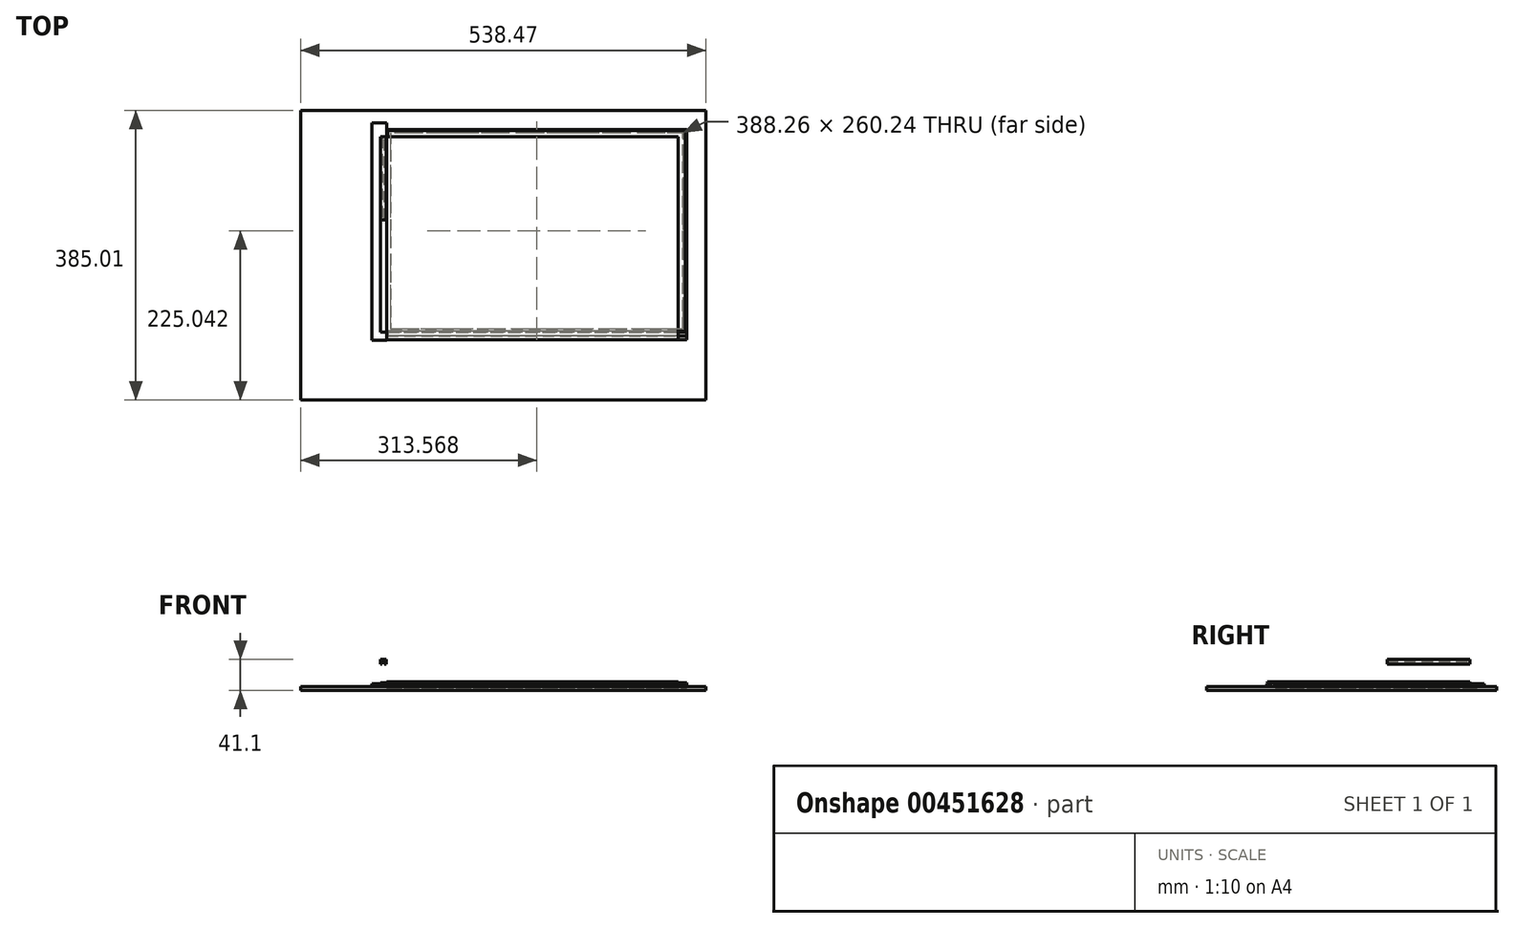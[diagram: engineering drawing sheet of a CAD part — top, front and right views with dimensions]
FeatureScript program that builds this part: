
annotation { "Feature Type Name" : "Feature", "Feature Type Description" : "" }
export const myFeature = defineFeature(function(context is Context, id is Id, definition is map)
    precondition{}
    {
        {
            var Q0;
            Q0=qCreatedBy(makeId("Top.planeOp"),FACE);
            var sketch = newSketch(context, id + "F0", { "sketchPlane" : qUnion([Q0])});
            skLineSegment(sketch, "E0", {"start": v(-190.36, 104.66) * mm, "end": v(205.64, 104.66) * mm});
            skLineSegment(sketch, "E1", {"start": v(205.64, 104.66) * mm, "end": v(205.64, -154.94) * mm});
            skLineSegment(sketch, "E2", {"start": v(205.64, -154.94) * mm, "end": v(-190.27, -154.94) * mm});
            skLineSegment(sketch, "E3", {"start": v(-190.27, -154.94) * mm, "end": v(-190.27, 104.66) * mm});
            skSolve(sketch);
        }
        {
            var Q0;
            Q0 = qSketchRegion(id + "F0", true);
            extrude(context, id + "F1", {"entities" : qUnion([Q0]), "depth" : 1.1 * mm});
        }
        {
            var Q0;
            Q0=makeQuery(id+"F1.opExtrude","CAP_FACE",FACE,{"disambiguationData":[OSD([sQuery(id+"F0.wireOp",EDGE,"E0"),sQuery(id+"F0.wireOp",EDGE,"E1"),sQuery(id+"F0.wireOp",EDGE,"E2"),sQuery(id+"F0.wireOp",EDGE,"E3")])],"isStart":false});
            var sketch = newSketch(context, id + "F2", { "sketchPlane" : qUnion([Q0])});
            skLineSegment(sketch, "E4", {"start": v(-181.96, 104.66) * mm, "end": v(-181.96, -164.94) * mm});
            skLineSegment(sketch, "E5", {"start": v(-181.96, -164.94) * mm, "end": v(205.64, -164.94) * mm});
            skLineSegment(sketch, "E6", {"start": v(205.64, -164.94) * mm, "end": v(205.64, 104.66) * mm});
            skLineSegment(sketch, "E7", {"start": v(205.64, 104.66) * mm, "end": v(-181.96, 104.66) * mm});
            skSolve(sketch);
        }
        {
            var Q0;
            Q0 = qSketchRegion(id + "F2", true);
            extrude(context, id + "F3", {"entities" : qUnion([Q0]), "depth" : 1.1 * mm});
        }
        {
            var Q0;
            Q0=makeQuery(id+"F1.opExtrude","CAP_FACE",FACE,{"disambiguationData":[OSD([sQuery(id+"F0.wireOp",EDGE,"E0"),sQuery(id+"F0.wireOp",EDGE,"E1"),sQuery(id+"F0.wireOp",EDGE,"E2"),sQuery(id+"F0.wireOp",EDGE,"E3")])],"isStart":true});
            cPlane(context, id + "F4", {"entities" : qUnion([Q0]), "cplaneType" : CPlaneType.OFFSET, "offset" : 9 * mm, "width" : 150 * mm, "height" : 150 * mm});
        }
        {
            var Q0;
            Q0=qCreatedBy(id+"F4.planeOp",FACE);
            var sketch = newSketch(context, id + "F5", { "sketchPlane" : qUnion([Q0])});
            skLineSegment(sketch, "E8", {"start": v(-296.19, 245.18) * mm, "end": v(242.28, 245.18) * mm});
            skLineSegment(sketch, "E9", {"start": v(242.28, 245.18) * mm, "end": v(242.28, -139.83) * mm});
            skLineSegment(sketch, "E10", {"start": v(242.28, -139.83) * mm, "end": v(-296.19, -139.83) * mm});
            skLineSegment(sketch, "E11", {"start": v(-296.19, -139.83) * mm, "end": v(-296.19, 245.18) * mm});
            skLineSegment(sketch, "E12", {"start": v(-181.87, 154.91) * mm, "end": v(216.63, 154.91) * mm});
            skLineSegment(sketch, "E13", {"start": v(216.63, 154.91) * mm, "end": v(216.63, -114.17) * mm});
            skLineSegment(sketch, "E14", {"start": v(216.63, -114.17) * mm, "end": v(-181.87, -114.17) * mm});
            skLineSegment(sketch, "E15", {"start": v(-181.87, -114.17) * mm, "end": v(-181.87, 154.91) * mm});
            skLineSegment(sketch, "E16", {"start": v(-176.75, 150.26) * mm, "end": v(211.5, 150.26) * mm});
            skLineSegment(sketch, "E17", {"start": v(211.5, 150.26) * mm, "end": v(211.5, -109.98) * mm});
            skLineSegment(sketch, "E18", {"start": v(211.5, -109.98) * mm, "end": v(-176.75, -109.98) * mm});
            skLineSegment(sketch, "E19", {"start": v(-176.75, -109.98) * mm, "end": v(-176.75, 150.26) * mm});
            skSolve(sketch);
        }
        {
            var Q0;
            Q0=makeQuery(id+"F5.imprint","IMPRINT",FACE,{"disambiguationData":[TD([[makeQuery(id+"F5.imprint","IMPRINT",EDGE,{"derivedFrom":sQuery(id+"F5.wireOp",EDGE,"E8")}),-1.0]])]});
            extrude(context, id + "F6", {"entities" : qUnion([Q0]), "oppositeDirection" : true, "depth" : 5 * mm});
        }
        {
            var Q0;
            Q0=makeQuery(id+"F5.imprint","IMPRINT",FACE,{"disambiguationData":[TD([[makeQuery(id+"F5.imprint","IMPRINT",EDGE,{"derivedFrom":sQuery(id+"F5.wireOp",EDGE,"E12")}),-1.0]])]});
            extrude(context, id + "F7", {"entities" : qUnion([Q0]), "operationType" : NewBodyOperationType.ADD, "oppositeDirection" : true, "depth" : 3 * mm});
        }
        {
            var Q0;
            Q0=makeQuery(id+"F6.opExtrude","CAP_FACE",FACE,{"disambiguationData":[OSD([sQuery(id+"F5.wireOp",EDGE,"E8"),sQuery(id+"F5.wireOp",EDGE,"E9"),sQuery(id+"F5.wireOp",EDGE,"E10"),sQuery(id+"F5.wireOp",EDGE,"E11"),sQuery(id+"F5.wireOp",EDGE,"E12"),sQuery(id+"F5.wireOp",EDGE,"E13"),sQuery(id+"F5.wireOp",EDGE,"E14"),sQuery(id+"F5.wireOp",EDGE,"E15")])],"isStart":false});
            var sketch = newSketch(context, id + "F8", { "sketchPlane" : qUnion([Q0])});
            skLineSegment(sketch, "E20", {"start": v(-181.87, -165.6) * mm, "end": v(-201.72, -165.6) * mm});
            skLineSegment(sketch, "E21", {"start": v(-201.72, -165.6) * mm, "end": v(-201.72, 123.46) * mm});
            skLineSegment(sketch, "E22", {"start": v(-201.72, 123.46) * mm, "end": v(-181.87, 123.46) * mm});
            skLineSegment(sketch, "E23", {"start": v(-181.87, 123.46) * mm, "end": v(-181.87, -165.6) * mm});
            skSolve(sketch);
        }
        {
            var Q0;
            {var subQ3=sQuery(id+"F8.wireOp",EDGE,"E20");Q0=makeQuery(id+"F8.imprint","IMPRINT",FACE,{"disambiguationData":[TD([[makeQuery(id+"F8.imprint","IMPRINT",EDGE,{"derivedFrom":subQ3}),-1.0]])]});}
            extrude(context, id + "F9", {"entities" : qUnion([Q0]), "depth" : 4 * mm});
        }
        {
            var Q0;
            Q0=makeQuery(id+"F6.opExtrude","CAP_FACE",FACE,{"disambiguationData":[OSD([sQuery(id+"F5.wireOp",EDGE,"E8"),sQuery(id+"F5.wireOp",EDGE,"E9"),sQuery(id+"F5.wireOp",EDGE,"E10"),sQuery(id+"F5.wireOp",EDGE,"E11"),sQuery(id+"F5.wireOp",EDGE,"E12"),sQuery(id+"F5.wireOp",EDGE,"E13"),sQuery(id+"F5.wireOp",EDGE,"E14"),sQuery(id+"F5.wireOp",EDGE,"E15")])],"isStart":false});
            var sketch = newSketch(context, id + "F10", { "sketchPlane" : qUnion([Q0])});
            skLineSegment(sketch, "E24", {"start": v(-181.55, -160.24) * mm, "end": v(216.92, -160.24) * mm});
            skLineSegment(sketch, "E25", {"start": v(216.92, -160.24) * mm, "end": v(216.92, -165.22) * mm});
            skLineSegment(sketch, "E26", {"start": v(216.92, -165.22) * mm, "end": v(-181.55, -165.22) * mm});
            skLineSegment(sketch, "E27", {"start": v(-181.55, -165.22) * mm, "end": v(-181.55, -160.24) * mm});
            skSolve(sketch);
        }
        {
            var Q0;
            Q0=makeQuery(id+"F10.imprint","IMPRINT",FACE,{"disambiguationData":[TD([[makeQuery(id+"F10.imprint","IMPRINT",EDGE,{"derivedFrom":sQuery(id+"F10.wireOp",EDGE,"E24")}),-1.0]])]});
            extrude(context, id + "F11", {"entities" : qUnion([Q0]), "depth" : 3 * mm});
        }
        {
            var Q0;
            Q0=makeQuery(id+"F7.opExtrude","CAP_FACE",FACE,{"disambiguationData":[OSD([sQuery(id+"F5.wireOp",EDGE,"E12"),sQuery(id+"F5.wireOp",EDGE,"E13"),sQuery(id+"F5.wireOp",EDGE,"E14"),sQuery(id+"F5.wireOp",EDGE,"E15"),sQuery(id+"F5.wireOp",EDGE,"E16"),sQuery(id+"F5.wireOp",EDGE,"E17"),sQuery(id+"F5.wireOp",EDGE,"E18"),sQuery(id+"F5.wireOp",EDGE,"E19")])],"isStart":false});
            var sketch = newSketch(context, id + "F12", { "sketchPlane" : qUnion([Q0])});
            skLineSegment(sketch, "E28", {"start": v(-180.71, 112.97) * mm, "end": v(215.2, 112.97) * mm});
            skLineSegment(sketch, "E29", {"start": v(215.2, 112.97) * mm, "end": v(215.2, -153.74) * mm});
            skLineSegment(sketch, "E30", {"start": v(215.2, -153.74) * mm, "end": v(-180.71, -153.74) * mm});
            skLineSegment(sketch, "E31", {"start": v(-180.71, -153.74) * mm, "end": v(-180.71, 112.97) * mm});
            skSolve(sketch);
        }
        {
            var Q0;
            Q0 = qSketchRegion(id + "F12", true);
            extrude(context, id + "F13", {"entities" : qUnion([Q0]), "depth" : 6 * mm});
        }
        {
            var Q0;
            Q0=makeQuery(id+"F6.opExtrude","CAP_FACE",FACE,{"disambiguationData":[OSD([sQuery(id+"F5.wireOp",EDGE,"E8"),sQuery(id+"F5.wireOp",EDGE,"E9"),sQuery(id+"F5.wireOp",EDGE,"E10"),sQuery(id+"F5.wireOp",EDGE,"E11"),sQuery(id+"F5.wireOp",EDGE,"E12"),sQuery(id+"F5.wireOp",EDGE,"E13"),sQuery(id+"F5.wireOp",EDGE,"E14"),sQuery(id+"F5.wireOp",EDGE,"E15")])],"isStart":false});
            var sketch = newSketch(context, id + "F14", { "sketchPlane" : qUnion([Q0])});
            skLineSegment(sketch, "E32", {"start": v(-180.01, -159.95) * mm, "end": v(-180.01, -155.07) * mm});
            skLineSegment(sketch, "E33", {"start": v(-180.01, -155.07) * mm, "end": v(216.6, -155.07) * mm});
            skLineSegment(sketch, "E34", {"start": v(216.6, -155.07) * mm, "end": v(216.6, -159.95) * mm});
            skLineSegment(sketch, "E35", {"start": v(216.6, -159.95) * mm, "end": v(-180.01, -159.95) * mm});
            skSolve(sketch);
        }
        {
            var Q0;
            Q0=makeQuery(id+"F14.imprint","IMPRINT",FACE,{"disambiguationData":[TD([[makeQuery(id+"F14.imprint","IMPRINT",EDGE,{"derivedFrom":sQuery(id+"F14.wireOp",EDGE,"E32")}),-1.0]])]});
            extrude(context, id + "F15", {"entities" : qUnion([Q0]), "depth" : 5 * mm});
        }
        {
            var Q0;
            Q0=makeQuery(id+"F1.opExtrude","CAP_FACE",FACE,{"disambiguationData":[OSD([sQuery(id+"F0.wireOp",EDGE,"E0"),sQuery(id+"F0.wireOp",EDGE,"E1"),sQuery(id+"F0.wireOp",EDGE,"E2"),sQuery(id+"F0.wireOp",EDGE,"E3")])],"isStart":false});
            cPlane(context, id + "F16", {"entities" : qUnion([Q0]), "cplaneType" : CPlaneType.OFFSET, "offset" : 25 * mm, "width" : 150 * mm, "height" : 150 * mm});
        }
        {
            var Q0;
            Q0=qCreatedBy(id+"F16.planeOp",FACE);
            var sketch = newSketch(context, id + "F17", { "sketchPlane" : qUnion([Q0])});
            skLineSegment(sketch, "E36", {"start": v(-185.07, 104.7) * mm, "end": v(-182.85, 104.7) * mm});
            skLineSegment(sketch, "E37", {"start": v(-182.85, 104.7) * mm, "end": v(-182.85, -5.55) * mm});
            skLineSegment(sketch, "E38", {"start": v(-182.85, -5.55) * mm, "end": v(-185.07, -5.55) * mm});
            skLineSegment(sketch, "E39", {"start": v(-185.07, -5.55) * mm, "end": v(-185.07, 104.7) * mm});
            skLineSegment(sketch, "E40", {"start": v(-190.26, 104.7) * mm, "end": v(-188.03, 104.7) * mm});
            skLineSegment(sketch, "E41", {"start": v(-188.03, 104.7) * mm, "end": v(-188.03, -5.55) * mm});
            skLineSegment(sketch, "E42", {"start": v(-188.03, -5.55) * mm, "end": v(-190.26, -5.55) * mm});
            skLineSegment(sketch, "E43", {"start": v(-190.26, -5.55) * mm, "end": v(-190.26, 104.7) * mm});
            skLineSegment(sketch, "E44", {"start": v(-185.07, 104.7) * mm, "end": v(-196.3, 104.7) * mm, "construction": true});
            skPoint(sketch, "E44.endSnap0", {"position": v(-189.14, 104.7) * mm});
            skLineSegment(sketch, "E45", {"start": v(-185.07, -5.55) * mm, "end": v(-195.64, -5.55) * mm, "construction": true});
            skSolve(sketch);
        }
        {
            var Q0;
            Q0=makeQuery(id+"F17.imprint","IMPRINT",FACE,{"disambiguationData":[TD([[makeQuery(id+"F17.imprint","IMPRINT",EDGE,{"derivedFrom":sQuery(id+"F17.wireOp",EDGE,"E36")}),-1.0]])]});
            var Q1;
            Q1=makeQuery(id+"F17.imprint","IMPRINT",FACE,{"disambiguationData":[TD([[makeQuery(id+"F17.imprint","IMPRINT",EDGE,{"derivedFrom":sQuery(id+"F17.wireOp",EDGE,"E40")}),-1.0]])]});
            extrude(context, id + "F18", {"entities" : qUnion([Q0, Q1]), "depth" : 3 * mm});
        }
        {
            var Q0;
            Q0=makeQuery(id+"F18.opExtrude","CAP_FACE",FACE,{"disambiguationData":[OSD([sQuery(id+"F17.wireOp",EDGE,"E36"),sQuery(id+"F17.wireOp",EDGE,"E37"),sQuery(id+"F17.wireOp",EDGE,"E38"),sQuery(id+"F17.wireOp",EDGE,"E39")])],"isStart":false});
            var sketch = newSketch(context, id + "F19", { "sketchPlane" : qUnion([Q0])});
            skLineSegment(sketch, "E46", {"start": v(-182.85, -5.55) * mm, "end": v(-190.26, -5.55) * mm});
            skLineSegment(sketch, "E47", {"start": v(-190.26, -5.55) * mm, "end": v(-190.26, 104.7) * mm});
            skLineSegment(sketch, "E48", {"start": v(-190.26, 104.7) * mm, "end": v(-182.85, 104.7) * mm});
            skLineSegment(sketch, "E49", {"start": v(-182.85, 104.7) * mm, "end": v(-182.85, -5.55) * mm});
            skSolve(sketch);
        }
        {
            var Q0;
            {var subQ2=sQuery(id+"F19.wireOp",EDGE,"E47");Q0=makeQuery(id+"F19.imprint","IMPRINT",FACE,{"disambiguationData":[TD([[makeQuery(id+"F19.imprint","IMPRINT",EDGE,{"derivedFrom":subQ2}),-1.0]])]});}
            var Q1;
            {var subQ0=sQuery(id+"F19.wireOp",EDGE,"E49");Q1=makeQuery(id+"F19.imprint","IMPRINT",FACE,{"disambiguationData":[TD([[makeQuery(id+"F19.imprint","IMPRINT",EDGE,{"derivedFrom":subQ0}),-1.0]])]});}
            extrude(context, id + "F20", {"entities" : qUnion([Q0, Q1]), "operationType" : NewBodyOperationType.ADD, "depth" : 3 * mm});
        }
    });
